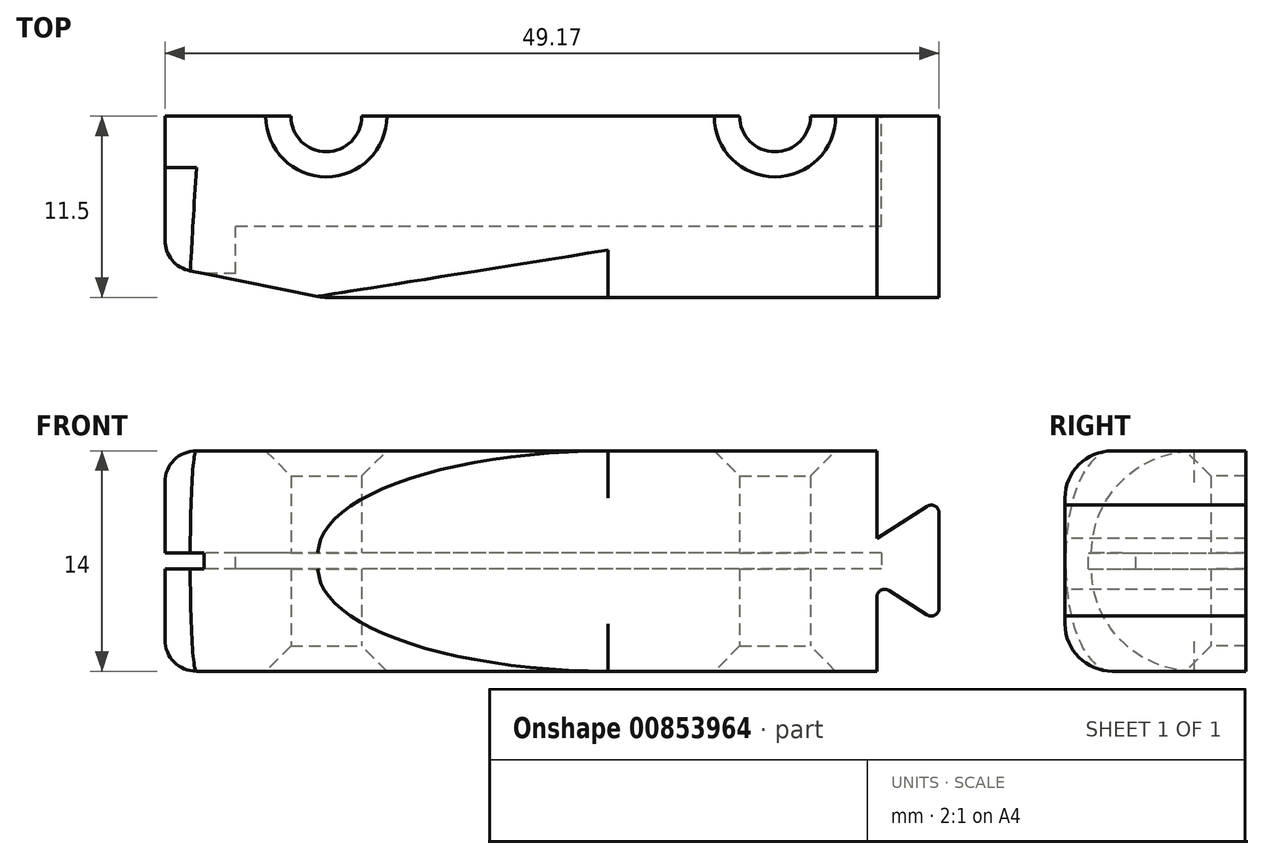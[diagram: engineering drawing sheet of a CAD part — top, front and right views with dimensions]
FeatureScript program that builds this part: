
annotation { "Feature Type Name" : "Feature", "Feature Type Description" : "" }
export const myFeature = defineFeature(function(context is Context, id is Id, definition is map)
    precondition{}
    {
        {
            var Q0;
            Q0=qCreatedBy(makeId("Top.planeOp"),FACE);
            var sketch = newSketch(context, id + "F0", { "sketchPlane" : qUnion([Q0])});
            skCircle(sketch, "E0", {"center": v(0, 0) * mm, "radius": 2.25 * mm});
            skCircle(sketch, "E1", {"center": v(-28.5, 0) * mm, "radius": 2.25 * mm});
            skPoint(sketch, "E2.start.orphan", {"position": v(86.29, 6) * mm});
            skLineSegment(sketch, "E3", {"start": v(-38.75, 11.5) * mm, "end": v(-38.75, -11.5) * mm});
            skLineSegment(sketch, "E4.bottom", {"start": v(-38.75, 11.5) * mm, "end": v(56.25, 11.5) * mm});
            skLineSegment(sketch, "E4.top", {"start": v(-38.75, -11.5) * mm, "end": v(56.25, -11.5) * mm});
            skLineSegment(sketch, "E4.right", {"start": v(56.25, 11.5) * mm, "end": v(56.25, -11.5) * mm});
            skLineSegment(sketch, "E5", {"start": v(6.25, 11.5) * mm, "end": v(6.25, -11.5) * mm, "construction": true});
            skSolve(sketch);
        }
        {
            var Q0;
            Q0=makeQuery(id+"F0.imprint","IMPRINT",FACE,{"disambiguationData":[TD([[makeQuery(id+"F0.imprint","IMPRINT",EDGE,{"derivedFrom":sQuery(id+"F0.wireOp",EDGE,"E0")}),-1.0]])]});
            extrude(context, id + "F1", {"entities" : qUnion([Q0]), "depth" : 14 * mm, "offsetDistance" : 25 * mm});
        }
        {
            var Q0;
            Q0=makeQuery(id+"F1.opExtrude","SWEPT_EDGE",EDGE,{"disambiguationData":[OSD([sQuery(id+"F0.wireOp",EDGE,"E4.bottom"),sQuery(id+"F0.wireOp",EDGE,"E3")])]});
            var Q1;
            Q1=makeQuery(id+"F1.opExtrude","SWEPT_EDGE",EDGE,{"disambiguationData":[OSD([sQuery(id+"F0.wireOp",EDGE,"E4.top"),sQuery(id+"F0.wireOp",EDGE,"E3")])]});
            chamfer(context, id + "F2", {"entities" : qUnion([Q0, Q1]), "chamferType" : ChamferType.TWO_OFFSETS, "width1" : 2 * mm, "oppositeDirection" : false, "width2" : 10 * mm, "tangentPropagation" : true});
        }
        {
            var Q0;
            {var subQ0=sQuery(id+"F0.wireOp",EDGE,"E3");var subQ1=sQuery(id+"F0.wireOp",EDGE,"E4.bottom");Q0=makeQuery(id+"F2.opChamfer","BLEND_EDGE",EDGE,{"blendedFrom":[makeQuery(id+"F1.opExtrude","SWEPT_EDGE",EDGE,{"disambiguationData":[OSD([subQ1,subQ0])]}),makeQuery(id+"F1.opExtrude","CAP_FACE",FACE,{"disambiguationData":[OSD([sQuery(id+"F0.wireOp",EDGE,"E0"),sQuery(id+"F0.wireOp",EDGE,"E1"),subQ1,sQuery(id+"F0.wireOp",EDGE,"E4.top"),subQ0,sQuery(id+"F0.wireOp",EDGE,"E4.right")])],"isStart":false})],"blendedInto":[makeQuery(id+"F1.opExtrude","CAP_FACE",FACE,{"disambiguationData":[OSD([sQuery(id+"F0.wireOp",EDGE,"E0"),sQuery(id+"F0.wireOp",EDGE,"E1"),subQ1,sQuery(id+"F0.wireOp",EDGE,"E4.top"),subQ0,sQuery(id+"F0.wireOp",EDGE,"E4.right")])],"isStart":false})]});}
            var Q1;
            {var subQ0=sQuery(id+"F0.wireOp",EDGE,"E3");var subQ1=sQuery(id+"F0.wireOp",EDGE,"E4.top");Q1=makeQuery(id+"F2.opChamfer","BLEND_EDGE",EDGE,{"blendedFrom":[makeQuery(id+"F1.opExtrude","SWEPT_EDGE",EDGE,{"disambiguationData":[OSD([subQ1,subQ0])]}),makeQuery(id+"F1.opExtrude","CAP_FACE",FACE,{"disambiguationData":[OSD([sQuery(id+"F0.wireOp",EDGE,"E0"),sQuery(id+"F0.wireOp",EDGE,"E1"),sQuery(id+"F0.wireOp",EDGE,"E4.bottom"),subQ1,subQ0,sQuery(id+"F0.wireOp",EDGE,"E4.right")])],"isStart":false})],"blendedInto":[makeQuery(id+"F1.opExtrude","CAP_FACE",FACE,{"disambiguationData":[OSD([sQuery(id+"F0.wireOp",EDGE,"E0"),sQuery(id+"F0.wireOp",EDGE,"E1"),sQuery(id+"F0.wireOp",EDGE,"E4.bottom"),subQ1,subQ0,sQuery(id+"F0.wireOp",EDGE,"E4.right")])],"isStart":false})]});}
            var Q2;
            {var subQ0=sQuery(id+"F0.wireOp",EDGE,"E3");var subQ1=sQuery(id+"F0.wireOp",EDGE,"E4.top");Q2=makeQuery(id+"F2.opChamfer","BLEND_EDGE",EDGE,{"blendedFrom":[makeQuery(id+"F1.opExtrude","SWEPT_EDGE",EDGE,{"disambiguationData":[OSD([subQ1,subQ0])]}),makeQuery(id+"F1.opExtrude","CAP_FACE",FACE,{"disambiguationData":[OSD([sQuery(id+"F0.wireOp",EDGE,"E0"),sQuery(id+"F0.wireOp",EDGE,"E1"),sQuery(id+"F0.wireOp",EDGE,"E4.bottom"),subQ1,subQ0,sQuery(id+"F0.wireOp",EDGE,"E4.right")])],"isStart":true})],"blendedInto":[makeQuery(id+"F1.opExtrude","CAP_FACE",FACE,{"disambiguationData":[OSD([sQuery(id+"F0.wireOp",EDGE,"E0"),sQuery(id+"F0.wireOp",EDGE,"E1"),sQuery(id+"F0.wireOp",EDGE,"E4.bottom"),subQ1,subQ0,sQuery(id+"F0.wireOp",EDGE,"E4.right")])],"isStart":true})]});}
            var Q3;
            {var subQ0=sQuery(id+"F0.wireOp",EDGE,"E3");var subQ1=sQuery(id+"F0.wireOp",EDGE,"E4.bottom");Q3=makeQuery(id+"F2.opChamfer","BLEND_EDGE",EDGE,{"blendedFrom":[makeQuery(id+"F1.opExtrude","SWEPT_EDGE",EDGE,{"disambiguationData":[OSD([subQ1,subQ0])]}),makeQuery(id+"F1.opExtrude","CAP_FACE",FACE,{"disambiguationData":[OSD([sQuery(id+"F0.wireOp",EDGE,"E0"),sQuery(id+"F0.wireOp",EDGE,"E1"),subQ1,sQuery(id+"F0.wireOp",EDGE,"E4.top"),subQ0,sQuery(id+"F0.wireOp",EDGE,"E4.right")])],"isStart":true})],"blendedInto":[makeQuery(id+"F1.opExtrude","CAP_FACE",FACE,{"disambiguationData":[OSD([sQuery(id+"F0.wireOp",EDGE,"E0"),sQuery(id+"F0.wireOp",EDGE,"E1"),subQ1,sQuery(id+"F0.wireOp",EDGE,"E4.top"),subQ0,sQuery(id+"F0.wireOp",EDGE,"E4.right")])],"isStart":true})]});}
            fillet(context, id + "F3", {"entities" : qUnion([Q0, Q1, Q2, Q3]), "radius" : 6.5 * mm, "allowEdgeOverflow" : false});
        }
        {
            var Q0;
            Q0=makeQuery(id+"F1.opExtrude","SWEPT_EDGE",EDGE,{"disambiguationData":[OSD([sQuery(id+"F0.wireOp",EDGE,"E4.bottom"),sQuery(id+"F0.wireOp",EDGE,"E4.right")])]});
            var Q1;
            Q1=makeQuery(id+"F1.opExtrude","SWEPT_EDGE",EDGE,{"disambiguationData":[OSD([sQuery(id+"F0.wireOp",EDGE,"E4.top"),sQuery(id+"F0.wireOp",EDGE,"E4.right")])]});
            chamfer(context, id + "F4", {"entities" : qUnion([Q0, Q1]), "chamferType" : ChamferType.TWO_OFFSETS, "width1" : 4 * mm, "oppositeDirection" : true, "width2" : 15 * mm});
        }
        {
            var Q0;
            Q0=makeQuery(id+"F1.opExtrude","CAP_EDGE",EDGE,{"disambiguationData":[OSD([sQuery(id+"F0.wireOp",EDGE,"E4.top")])],"isStart":true});
            var Q1;
            Q1=makeQuery(id+"F1.opExtrude","CAP_EDGE",EDGE,{"disambiguationData":[OSD([sQuery(id+"F0.wireOp",EDGE,"E4.bottom")])],"isStart":true});
            var Q2;
            {var subQ0=sQuery(id+"F0.wireOp",EDGE,"E4.right");var subQ1=sQuery(id+"F0.wireOp",EDGE,"E4.top");Q2=makeQuery(id+"F4.opChamfer","BLEND_EDGE",EDGE,{"blendedFrom":[makeQuery(id+"F1.opExtrude","SWEPT_EDGE",EDGE,{"disambiguationData":[OSD([subQ1,subQ0])]}),makeQuery(id+"F1.opExtrude","CAP_FACE",FACE,{"disambiguationData":[OSD([sQuery(id+"F0.wireOp",EDGE,"E0"),sQuery(id+"F0.wireOp",EDGE,"E1"),sQuery(id+"F0.wireOp",EDGE,"E4.bottom"),subQ1,sQuery(id+"F0.wireOp",EDGE,"E3"),subQ0])],"isStart":false})],"blendedInto":[makeQuery(id+"F1.opExtrude","CAP_FACE",FACE,{"disambiguationData":[OSD([sQuery(id+"F0.wireOp",EDGE,"E0"),sQuery(id+"F0.wireOp",EDGE,"E1"),sQuery(id+"F0.wireOp",EDGE,"E4.bottom"),subQ1,sQuery(id+"F0.wireOp",EDGE,"E3"),subQ0])],"isStart":false})]});}
            var Q3;
            {var subQ0=sQuery(id+"F0.wireOp",EDGE,"E4.right");var subQ1=sQuery(id+"F0.wireOp",EDGE,"E4.bottom");Q3=makeQuery(id+"F4.opChamfer","BLEND_EDGE",EDGE,{"blendedFrom":[makeQuery(id+"F1.opExtrude","SWEPT_EDGE",EDGE,{"disambiguationData":[OSD([subQ1,subQ0])]}),makeQuery(id+"F1.opExtrude","CAP_FACE",FACE,{"disambiguationData":[OSD([sQuery(id+"F0.wireOp",EDGE,"E0"),sQuery(id+"F0.wireOp",EDGE,"E1"),subQ1,sQuery(id+"F0.wireOp",EDGE,"E4.top"),sQuery(id+"F0.wireOp",EDGE,"E3"),subQ0])],"isStart":false})],"blendedInto":[makeQuery(id+"F1.opExtrude","CAP_FACE",FACE,{"disambiguationData":[OSD([sQuery(id+"F0.wireOp",EDGE,"E0"),sQuery(id+"F0.wireOp",EDGE,"E1"),subQ1,sQuery(id+"F0.wireOp",EDGE,"E4.top"),sQuery(id+"F0.wireOp",EDGE,"E3"),subQ0])],"isStart":false})]});}
            var Q4;
            {var subQ0=sQuery(id+"F0.wireOp",EDGE,"E4.right");var subQ1=sQuery(id+"F0.wireOp",EDGE,"E4.bottom");Q4=makeQuery(id+"F4.opChamfer","BLEND_EDGE",EDGE,{"blendedFrom":[makeQuery(id+"F1.opExtrude","SWEPT_EDGE",EDGE,{"disambiguationData":[OSD([subQ1,subQ0])]}),makeQuery(id+"F1.opExtrude","CAP_FACE",FACE,{"disambiguationData":[OSD([sQuery(id+"F0.wireOp",EDGE,"E0"),sQuery(id+"F0.wireOp",EDGE,"E1"),subQ1,sQuery(id+"F0.wireOp",EDGE,"E4.top"),sQuery(id+"F0.wireOp",EDGE,"E3"),subQ0])],"isStart":true})],"blendedInto":[makeQuery(id+"F1.opExtrude","CAP_FACE",FACE,{"disambiguationData":[OSD([sQuery(id+"F0.wireOp",EDGE,"E0"),sQuery(id+"F0.wireOp",EDGE,"E1"),subQ1,sQuery(id+"F0.wireOp",EDGE,"E4.top"),sQuery(id+"F0.wireOp",EDGE,"E3"),subQ0])],"isStart":true})]});}
            var Q5;
            {var subQ0=sQuery(id+"F0.wireOp",EDGE,"E4.right");var subQ1=sQuery(id+"F0.wireOp",EDGE,"E4.top");Q5=makeQuery(id+"F4.opChamfer","BLEND_EDGE",EDGE,{"blendedFrom":[makeQuery(id+"F1.opExtrude","SWEPT_EDGE",EDGE,{"disambiguationData":[OSD([subQ1,subQ0])]}),makeQuery(id+"F1.opExtrude","CAP_FACE",FACE,{"disambiguationData":[OSD([sQuery(id+"F0.wireOp",EDGE,"E0"),sQuery(id+"F0.wireOp",EDGE,"E1"),sQuery(id+"F0.wireOp",EDGE,"E4.bottom"),subQ1,sQuery(id+"F0.wireOp",EDGE,"E3"),subQ0])],"isStart":true})],"blendedInto":[makeQuery(id+"F1.opExtrude","CAP_FACE",FACE,{"disambiguationData":[OSD([sQuery(id+"F0.wireOp",EDGE,"E0"),sQuery(id+"F0.wireOp",EDGE,"E1"),sQuery(id+"F0.wireOp",EDGE,"E4.bottom"),subQ1,sQuery(id+"F0.wireOp",EDGE,"E3"),subQ0])],"isStart":true})]});}
            var Q6;
            Q6=makeQuery(id+"F1.opExtrude","SWEPT_FACE",FACE,{"disambiguationData":[OSD([sQuery(id+"F0.wireOp",EDGE,"E4.right")])]});
            fillet(context, id + "F5", {"entities" : qUnion([Q0, Q1, Q2, Q3, Q4, Q5, Q6]), "radius" : 3 * mm, "tangentPropagation" : true, "allowEdgeOverflow" : false});
        }
        {
            var Q0;
            Q0=makeQuery(id+"F1.opExtrude","SWEPT_FACE",FACE,{"disambiguationData":[OSD([sQuery(id+"F0.wireOp",EDGE,"E3")])]});
            fillet(context, id + "F6", {"entities" : qUnion([Q0]), "radius" : 2 * mm, "tangentPropagation" : true, "allowEdgeOverflow" : false});
        }
        {
            var Q0;
            Q0=makeQuery(id+"F1.opExtrude","CAP_FACE",FACE,{"disambiguationData":[OSD([sQuery(id+"F0.wireOp",EDGE,"E0"),sQuery(id+"F0.wireOp",EDGE,"E1"),sQuery(id+"F0.wireOp",EDGE,"E4.bottom"),sQuery(id+"F0.wireOp",EDGE,"E4.top"),sQuery(id+"F0.wireOp",EDGE,"E3"),sQuery(id+"F0.wireOp",EDGE,"E4.right")])],"isStart":false});
            var sketch = newSketch(context, id + "F7", { "sketchPlane" : qUnion([Q0])});
            skLineSegment(sketch, "E6.bottom", {"start": v(-41.82, -15.17) * mm, "end": v(6.47, -15.17) * mm});
            skLineSegment(sketch, "E6.top", {"start": v(-41.82, 0) * mm, "end": v(6.47, 0) * mm});
            skLineSegment(sketch, "E6.left", {"start": v(-41.82, -15.17) * mm, "end": v(-41.82, 0) * mm});
            skLineSegment(sketch, "E6.right", {"start": v(6.47, -15.17) * mm, "end": v(6.47, 0) * mm});
            skSolve(sketch);
        }
        {
            var Q0;
            Q0=qSketchRegion(id+"F7",true);
            extrude(context, id + "F8", {"entities" : qUnion([Q0]), "operationType" : NewBodyOperationType.INTERSECT, "oppositeDirection" : true, "depth" : 25 * mm, "offsetDistance" : 25 * mm});
        }
        {
            var Q0;
            Q0=makeQuery(id+"F1.opExtrude","SWEPT_FACE",FACE,{"disambiguationData":[OSD([sQuery(id+"F0.wireOp",EDGE,"E4.top")])]});
            var sketch = newSketch(context, id + "F9", { "sketchPlane" : qUnion([Q0])});
            skLineSegment(sketch, "E7", {"start": v(6.47, 8.43) * mm, "end": v(10.42, 10.97) * mm});
            skLineSegment(sketch, "E8", {"start": v(10.42, 10.97) * mm, "end": v(10.42, 3.09) * mm});
            skLineSegment(sketch, "E9", {"start": v(10.42, 3.09) * mm, "end": v(6.47, 5.63) * mm});
            skSolve(sketch);
        }
        {
            var Q0;
            {var subQ0=sQuery(id+"F9.wireOp",EDGE,"E7");Q0=makeQuery(id+"F9.imprint","IMPRINT",FACE,{"disambiguationData":[TD([[makeQuery(id+"F9.imprint","IMPRINT",EDGE,{"derivedFrom":subQ0}),-1.0]])]});}
            extrude(context, id + "F10", {"entities" : qUnion([Q0]), "operationType" : NewBodyOperationType.ADD, "oppositeDirection" : true, "depth" : 11.5 * mm, "offsetDistance" : 25 * mm});
        }
        {
            var Q0;
            Q0=makeQuery(id+"F10.opExtrude","SWEPT_EDGE",EDGE,{"disambiguationData":[OSD([sQuery(id+"F0.wireOp",EDGE,"E4.top"),sQuery(id+"F7.wireOp",EDGE,"E6.right"),sQuery(id+"F9.wireOp",EDGE,"E7")])]});
            var Q1;
            Q1=makeQuery(id+"F10.opExtrude","SWEPT_EDGE",EDGE,{"disambiguationData":[OSD([sQuery(id+"F0.wireOp",EDGE,"E4.top"),sQuery(id+"F7.wireOp",EDGE,"E6.right"),sQuery(id+"F9.wireOp",EDGE,"E9")])]});
            var Q2;
            Q2=makeQuery(id+"F10.opExtrude","SWEPT_EDGE",EDGE,{"disambiguationData":[OSD([sQuery(id+"F9.wireOp",EDGE,"E7"),sQuery(id+"F9.wireOp",EDGE,"E8")])]});
            var Q3;
            Q3=makeQuery(id+"F10.opExtrude","SWEPT_EDGE",EDGE,{"disambiguationData":[OSD([sQuery(id+"F9.wireOp",EDGE,"E8"),sQuery(id+"F9.wireOp",EDGE,"E9")])]});
            fillet(context, id + "F11", {"entities" : qUnion([Q0, Q1, Q2, Q3]), "radius" : .5 * mm, "allowEdgeOverflow" : false});
        }
        {
            var Q0;
            Q0=makeQuery(id+"F1.opExtrude","SWEPT_FACE",FACE,{"disambiguationData":[OSD([sQuery(id+"F0.wireOp",EDGE,"E3")])]});
            var sketch = newSketch(context, id + "F12", { "sketchPlane" : qUnion([Q0])});
            skLineSegment(sketch, "E10.bottom", {"start": v(10, 7.5) * mm, "end": v(-10, 7.5) * mm});
            skLineSegment(sketch, "E10.top", {"start": v(10, 6.5) * mm, "end": v(-10, 6.5) * mm});
            skLineSegment(sketch, "E10.left", {"start": v(10, 7.5) * mm, "end": v(10, 6.5) * mm});
            skLineSegment(sketch, "E10.right", {"start": v(-10, 7.5) * mm, "end": v(-10, 6.5) * mm});
            skSolve(sketch);
        }
        {
            var Q0;
            Q0 = qSketchRegion(id + "F12", true);
            extrude(context, id + "F13", {"entities" : qUnion([Q0]), "operationType" : NewBodyOperationType.REMOVE, "oppositeDirection" : true, "depth" : 4.5 * mm, "offsetDistance" : 25 * mm});
        }
        {
            var Q0;
            Q0=makeQuery(id+"F13.boolean.opBoolean","COPY",FACE,{"derivedFrom":makeQuery(id+"F13.opExtrude","CAP_FACE",FACE,{"disambiguationData":[OSD([sQuery(id+"F12.wireOp",EDGE,"E10.bottom"),sQuery(id+"F12.wireOp",EDGE,"E10.top"),sQuery(id+"F12.wireOp",EDGE,"E10.left"),sQuery(id+"F12.wireOp",EDGE,"E10.right")])],"isStart":false})});
            var sketch = newSketch(context, id + "F14", { "sketchPlane" : qUnion([Q0])});
            skLineSegment(sketch, "E11.bottom", {"start": v(0, 6.5) * mm, "end": v(7, 6.5) * mm});
            skLineSegment(sketch, "E11.top", {"start": v(0, 7.5) * mm, "end": v(7, 7.5) * mm});
            skLineSegment(sketch, "E11.left", {"start": v(0, 6.5) * mm, "end": v(0, 7.5) * mm});
            skLineSegment(sketch, "E11.right", {"start": v(7, 6.5) * mm, "end": v(7, 7.5) * mm});
            skSolve(sketch);
        }
        {
            var Q0;
            Q0 = qSketchRegion(id + "F14", true);
            extrude(context, id + "F15", {"entities" : qUnion([Q0]), "operationType" : NewBodyOperationType.REMOVE, "oppositeDirection" : true, "depth" : 41 * mm, "offsetDistance" : 25 * mm});
        }
        {
            var Q0;
            Q0=makeQuery(id+"F1.opExtrude","CAP_EDGE",EDGE,{"disambiguationData":[OSD([sQuery(id+"F0.wireOp",EDGE,"E0")])],"isStart":false});
            var Q1;
            Q1=makeQuery(id+"F1.opExtrude","CAP_EDGE",EDGE,{"disambiguationData":[OSD([sQuery(id+"F0.wireOp",EDGE,"E1")])],"isStart":false});
            var Q2;
            Q2=makeQuery(id+"F1.opExtrude","CAP_EDGE",EDGE,{"disambiguationData":[OSD([sQuery(id+"F0.wireOp",EDGE,"E1")])],"isStart":true});
            var Q3;
            Q3=makeQuery(id+"F1.opExtrude","CAP_EDGE",EDGE,{"disambiguationData":[OSD([sQuery(id+"F0.wireOp",EDGE,"E0")])],"isStart":true});
            chamfer(context, id + "F16", {"entities" : qUnion([Q0, Q1, Q2, Q3]), "width" : 1.6 * mm, "tangentPropagation" : true});
        }
    });
